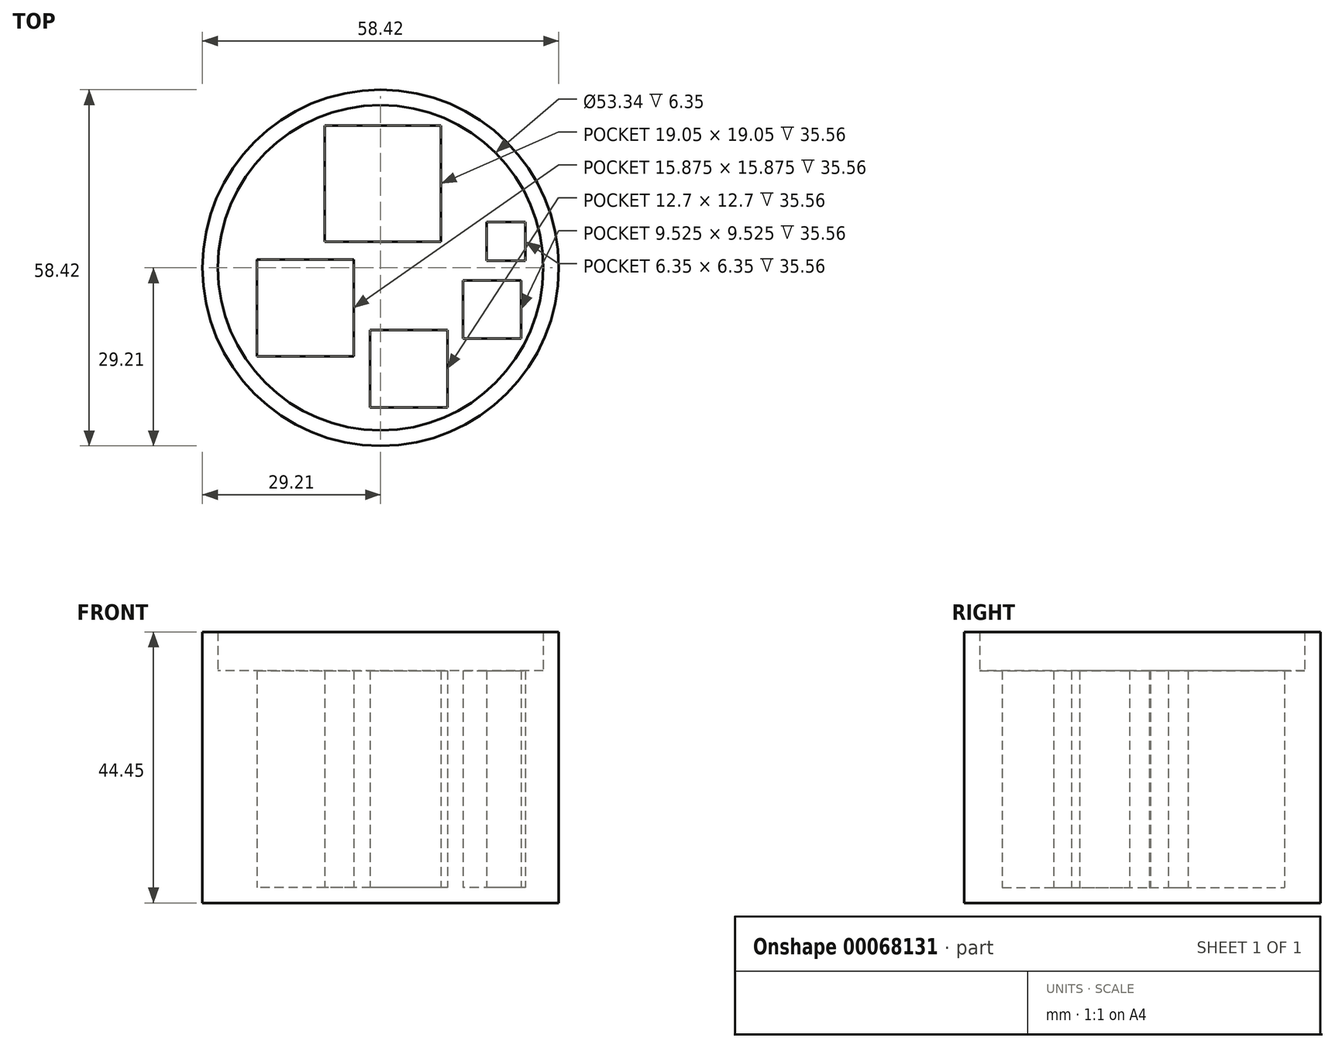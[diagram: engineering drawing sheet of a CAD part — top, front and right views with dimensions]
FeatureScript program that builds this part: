
annotation { "Feature Type Name" : "Feature", "Feature Type Description" : "" }
export const myFeature = defineFeature(function(context is Context, id is Id, definition is map)
    precondition{}
    {
        {
            var Q0;
            Q0=qCreatedBy(makeId("Top.planeOp"),FACE);
            var sketch = newSketch(context, id + "F0", { "sketchPlane" : qUnion([Q0])});
            skCircle(sketch, "E0", {"center": v(0, 0) * mm, "radius": 26.67 * mm});
            skCircle(sketch, "E1", {"center": v(0, 0) * mm, "radius": 27.94 * mm});
            skCircle(sketch, "E2", {"center": v(0, 0) * mm, "radius": 29.21 * mm});
            skLineSegment(sketch, "E3.bottom", {"start": v(-9.14, 23.34) * mm, "end": v(9.9, 23.34) * mm});
            skLineSegment(sketch, "E3.top", {"start": v(-9.14, 4.3) * mm, "end": v(9.9, 4.3) * mm});
            skLineSegment(sketch, "E3.left", {"start": v(-9.14, 23.34) * mm, "end": v(-9.14, 4.3) * mm});
            skLineSegment(sketch, "E3.right", {"start": v(9.9, 23.34) * mm, "end": v(9.9, 4.3) * mm});
            skLineSegment(sketch, "E4.bottom", {"start": v(-20.27, 1.35) * mm, "end": v(-4.4, 1.35) * mm});
            skLineSegment(sketch, "E4.top", {"start": v(-20.27, -14.53) * mm, "end": v(-4.4, -14.53) * mm});
            skLineSegment(sketch, "E4.left", {"start": v(-20.27, 1.35) * mm, "end": v(-20.27, -14.53) * mm});
            skLineSegment(sketch, "E4.right", {"start": v(-4.4, 1.35) * mm, "end": v(-4.4, -14.53) * mm});
            skLineSegment(sketch, "E5.bottom", {"start": v(-1.76, -10.23) * mm, "end": v(10.94, -10.23) * mm});
            skLineSegment(sketch, "E5.top", {"start": v(-1.76, -22.93) * mm, "end": v(10.94, -22.93) * mm});
            skLineSegment(sketch, "E5.left", {"start": v(-1.76, -10.23) * mm, "end": v(-1.76, -22.93) * mm});
            skLineSegment(sketch, "E5.right", {"start": v(10.94, -10.23) * mm, "end": v(10.94, -22.93) * mm});
            skLineSegment(sketch, "E6.bottom", {"start": v(13.49, -2.05) * mm, "end": v(23.01, -2.05) * mm});
            skLineSegment(sketch, "E6.top", {"start": v(13.49, -11.57) * mm, "end": v(23.01, -11.57) * mm});
            skLineSegment(sketch, "E6.left", {"start": v(13.49, -2.05) * mm, "end": v(13.49, -11.57) * mm});
            skLineSegment(sketch, "E6.right", {"start": v(23.01, -2.05) * mm, "end": v(23.01, -11.57) * mm});
            skLineSegment(sketch, "E7.bottom", {"start": v(17.4, 7.53) * mm, "end": v(23.75, 7.53) * mm});
            skLineSegment(sketch, "E7.top", {"start": v(17.4, 1.18) * mm, "end": v(23.75, 1.18) * mm});
            skLineSegment(sketch, "E7.left", {"start": v(17.4, 7.53) * mm, "end": v(17.4, 1.18) * mm});
            skLineSegment(sketch, "E7.right", {"start": v(23.75, 7.53) * mm, "end": v(23.75, 1.18) * mm});
            skSolve(sketch);
        }
        {
            var Q0;
            Q0=makeQuery(id+"F0.imprint","IMPRINT",FACE,{"disambiguationData":[TD([[makeQuery(id+"F0.imprint","IMPRINT",EDGE,{"derivedFrom":sQuery(id+"F0.wireOp",EDGE,"E0")}),1.0]])]});
            var Q1;
            Q1=makeQuery(id+"F0.imprint","IMPRINT",FACE,{"disambiguationData":[TD([[makeQuery(id+"F0.imprint","IMPRINT",EDGE,{"derivedFrom":sQuery(id+"F0.wireOp",EDGE,"E3.bottom")}),-1.0]])]});
            var Q2;
            Q2=makeQuery(id+"F0.imprint","IMPRINT",FACE,{"disambiguationData":[TD([[makeQuery(id+"F0.imprint","IMPRINT",EDGE,{"derivedFrom":sQuery(id+"F0.wireOp",EDGE,"E4.bottom")}),-1.0]])]});
            var Q3;
            Q3=makeQuery(id+"F0.imprint","IMPRINT",FACE,{"disambiguationData":[TD([[makeQuery(id+"F0.imprint","IMPRINT",EDGE,{"derivedFrom":sQuery(id+"F0.wireOp",EDGE,"E5.bottom")}),-1.0]])]});
            var Q4;
            Q4=makeQuery(id+"F0.imprint","IMPRINT",FACE,{"disambiguationData":[TD([[makeQuery(id+"F0.imprint","IMPRINT",EDGE,{"derivedFrom":sQuery(id+"F0.wireOp",EDGE,"E6.bottom")}),-1.0]])]});
            var Q5;
            Q5=makeQuery(id+"F0.imprint","IMPRINT",FACE,{"disambiguationData":[TD([[makeQuery(id+"F0.imprint","IMPRINT",EDGE,{"derivedFrom":sQuery(id+"F0.wireOp",EDGE,"E7.bottom")}),-1.0]])]});
            extrude(context, id + "F1", {"entities" : qUnion([Q0, Q1, Q2, Q3, Q4, Q5]), "depth" : 2.54 * mm});
        }
        {
            var Q0;
            Q0=makeQuery(id+"F0.imprint","IMPRINT",FACE,{"disambiguationData":[TD([[makeQuery(id+"F0.imprint","IMPRINT",EDGE,{"derivedFrom":sQuery(id+"F0.wireOp",EDGE,"E0")}),-1.0]])]});
            extrude(context, id + "F2", {"entities" : qUnion([Q0]), "operationType" : NewBodyOperationType.ADD, "depth" : 44.45 * mm});
        }
        {
            var Q0;
            Q0=makeQuery(id+"F0.imprint","IMPRINT",FACE,{"disambiguationData":[TD([[makeQuery(id+"F0.imprint","IMPRINT",EDGE,{"derivedFrom":sQuery(id+"F0.wireOp",EDGE,"E1")}),-1.0]])]});
            var Q1;
            Q1=makeQuery(id+"F0.imprint","IMPRINT",FACE,{"disambiguationData":[TD([[makeQuery(id+"F0.imprint","IMPRINT",EDGE,{"derivedFrom":sQuery(id+"F0.wireOp",EDGE,"E0")}),1.0]])]});
            extrude(context, id + "F3", {"entities" : qUnion([Q0, Q1]), "operationType" : NewBodyOperationType.ADD, "depth" : 38.1 * mm});
        }
        {
            var Q0;
            Q0=makeQuery(id+"F0.imprint","IMPRINT",FACE,{"disambiguationData":[TD([[makeQuery(id+"F0.imprint","IMPRINT",EDGE,{"derivedFrom":sQuery(id+"F0.wireOp",EDGE,"E0")}),1.0]])]});
            var Q1;
            Q1=makeQuery(id+"F0.imprint","IMPRINT",FACE,{"disambiguationData":[TD([[makeQuery(id+"F0.imprint","IMPRINT",EDGE,{"derivedFrom":sQuery(id+"F0.wireOp",EDGE,"E4.bottom")}),-1.0]])]});
            var Q2;
            Q2=makeQuery(id+"F0.imprint","IMPRINT",FACE,{"disambiguationData":[TD([[makeQuery(id+"F0.imprint","IMPRINT",EDGE,{"derivedFrom":sQuery(id+"F0.wireOp",EDGE,"E5.bottom")}),-1.0]])]});
            var Q3;
            Q3=makeQuery(id+"F0.imprint","IMPRINT",FACE,{"disambiguationData":[TD([[makeQuery(id+"F0.imprint","IMPRINT",EDGE,{"derivedFrom":sQuery(id+"F0.wireOp",EDGE,"E6.bottom")}),-1.0]])]});
            var Q4;
            Q4=makeQuery(id+"F0.imprint","IMPRINT",FACE,{"disambiguationData":[TD([[makeQuery(id+"F0.imprint","IMPRINT",EDGE,{"derivedFrom":sQuery(id+"F0.wireOp",EDGE,"E7.bottom")}),-1.0]])]});
            var Q5;
            Q5=makeQuery(id+"F0.imprint","IMPRINT",FACE,{"disambiguationData":[TD([[makeQuery(id+"F0.imprint","IMPRINT",EDGE,{"derivedFrom":sQuery(id+"F0.wireOp",EDGE,"E3.bottom")}),-1.0]])]});
            extrude(context, id + "F4", {"entities" : qUnion([Q0, Q1, Q2, Q3, Q4, Q5]), "depth" : 2.54 * mm});
        }
        {
            var Q0;
            Q0=makeQuery(id+"F0.imprint","IMPRINT",FACE,{"disambiguationData":[TD([[makeQuery(id+"F0.imprint","IMPRINT",EDGE,{"derivedFrom":sQuery(id+"F0.wireOp",EDGE,"E0")}),-1.0]])]});
            extrude(context, id + "F5", {"entities" : qUnion([Q0]), "operationType" : NewBodyOperationType.ADD, "depth" : 38.1 * mm});
        }
        {
            var Q0;
            Q0=makeQuery(id+"F0.imprint","IMPRINT",FACE,{"disambiguationData":[TD([[makeQuery(id+"F0.imprint","IMPRINT",EDGE,{"derivedFrom":sQuery(id+"F0.wireOp",EDGE,"E1")}),-1.0]])]});
            extrude(context, id + "F6", {"entities" : qUnion([Q0]), "operationType" : NewBodyOperationType.ADD, "depth" : 44.45 * mm});
        }
    });
